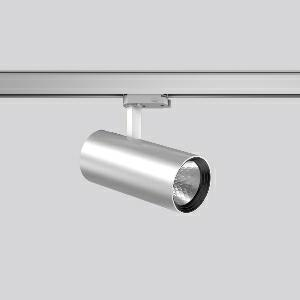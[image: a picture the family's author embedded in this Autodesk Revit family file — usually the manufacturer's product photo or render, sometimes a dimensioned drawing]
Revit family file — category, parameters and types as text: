
# Revit family: deecos_s_mini_742196_004_1_a926
name_source: partatom
category: Lighting Fixtures
units: mm (PartAtom-declared; Revit-internal decimal feet)

## family parameters
Cut with Voids When Loaded = No
Host = Face
Light Source = No
Part Type = Normal
Room Calculation Point = No
Round Connector Dimension = Use Diameter
Shared = No

## types (1)
- DEECOS S mini (1 x LED Modul 940, 2600 lm, 4000)
    Apparent Load = 20 VA
    Approval mark = CE
    CIE Flux Codes = 99 100 100 100 100
    Color Rendering = 92
    Color Temperature = 4000
    Default Elevation = 1800 mm
    Description = Series: DEECOS S mini
LED surface-mounted projector in modern design with no visible cooling ribs. Housing: die-cast aluminium, powder-coated. Rotation range: 356°. Swivel range: 90°. Black plastic ring and recessed LED to prevent glare from the side. Optical assembly with reflector made of MIRO-Silver with 98% total light reflection for outstanding efficiency - can be changed without tools. Best colour rendering index Ra>90. With multi adaptor for 3-circuit tracks 230 V. Suitable for Track on ceiling, Wall track. High quality converter without flickering and stroboscopic effect. The following accessories can be mounted without use of tools: interchangeable lenses, decorative glasses, honeycomb louvre, clear and frosted diffusers, white interchangeable plastic ring. 
Colour: silver
Diameter: 87 mm
Height: 214 mm
Lamp: LED
Socket: without socket
Colour temperature: 4000K
Colour rendering index (CRI): 92
System power: 20 W
Rated luminous flux: 2600 lm
Luminous efficiency: 130 lm/W
Control gear: Regulated power supply
Protection class: I
Type of protection: IP 20
    Height = 214 mm
    Lamp = 1 x LED Modul 940
    Lamp Light Flux = 2600 lm
    Lamp count = 1
    Length = 87 mm
    Lifetime = 50000 h
    Luminous efficacy = 130 lm/W
    Manufacturer = RZB
    ModVariant = No
    Model = 742196.004.1
    Mounting Place = Ceiling
    Mounting Type = Rail mounted
    Number of Poles = 1
    OnlyDefault = Yes
    Power Factor = 1
    Product Name = DEECOS S mini
    Product group = Track mounted projectors
    ProductGroupID = 301
    Protection Class = Protection class I
    Protection Degree = IP 20
    RLX_Detail_Level = 1
    RLX_Emergency_Light_Flux = 0 lm
    RLX_Emergency_Type = 0
    RLX_Emergency_Type_DB = No
    RlxData = <blob elided: 37225 chars, md5=0cde616f>
    Socket = socket
    Standby Power = 0 W
    System Light Flux = 2600 lm
    System Power = 20 W
    Type Comments = Product without accessories
    Type Image = 741926.004.jpg
    URL = http://relux.com
    VarID = ---
    Voltage = 230 V
    Voltage Range = 220-240 V
    Weight = 0.00 kg
    Width = 0 mm  [stored 0 ft]

note: [stored X ft] marks values corroborated as IEEE doubles in the binary element streams (Revit-internal decimal feet)

## geometry (parser evidence)
native form markers: Blend x4, Sweep x10
no freeform markers — native parametric forms only
